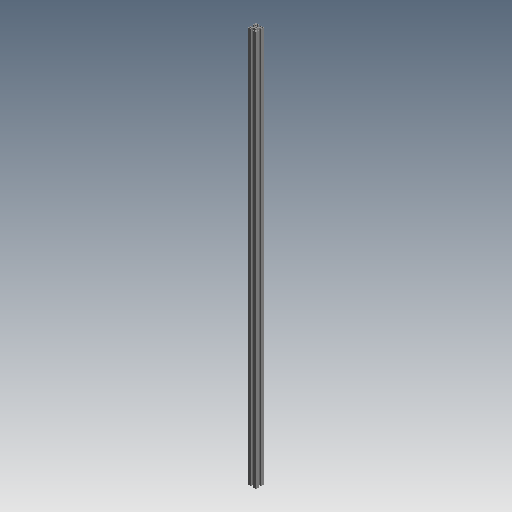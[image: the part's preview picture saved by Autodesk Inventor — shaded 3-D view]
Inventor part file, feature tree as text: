
AUTODESK INVENTOR PART (.ipt)
format: ipt  version: 2020 (Build 240168000, 168)  size: 211,968 bytes
history: native  units: mm (DEFAULTED — no unit token found)
features: other x21, sketch x3, hole x2, extrude x1, pattern_linear x1
ambient origin geometry x8: Origin, YZ Plane, XZ Plane, XY Plane, X Axis, Y Axis, Z Axis, Center Point
bodies: Solid1 (feature_tree)
feature tree (28):
  extrude  "Extrusion1"  Depth=1500.0mm
  hole  "Hole1"  [1 undecoded]
  hole  "Hole2"  [1 undecoded]
  pattern_linear  "Rectangular Pattern1"  [2 undecoded]
  other  "C1_XY"
  other  "C1_YZ"
  other  "C1_ZX"
  other  "C1_X"
  other  "C1_Y"
  other  "C1_Z"
  other  "C1_Center"
  other  "to_frame_cap1_XY"
  other  "to_frame_cap1_YZ"
  other  "to_frame_cap1_ZX"
  other  "to_frame_cap1_X"
  other  "to_frame_cap1_Y"
  other  "to_frame_cap1_Z"
  other  "to_frame_cap1_Center"
  other  "to_frame_cap2_XY"
  other  "to_frame_cap2_YZ"
  other  "to_frame_cap2_ZX"
  other  "to_frame_cap2_X"
  other  "to_frame_cap2_Y"
  other  "to_frame_cap2_Z"
  other  "to_frame_cap2_Center"
  sketch  "Sketch_1"  dims[d0=1500.0mm d1=0.0mm]
  sketch  "Sketch2"  dims[d2=6.8mm d3=6.0mm d4=4.0mm d5=2.0mm d6=90.0deg d7=1500.0mm d8=0.0mm]
  sketch  "Sketch3"  dims[d9=4.2mm d10=6.0mm d11=4.0mm d12=2.0mm d13=90.0deg d14=1500.0mm d15=0.0mm d16=20.0mm d18=23.2mm d19=20.0mm d21=23.2mm d22=0.0mm d23=0.0mm d24=0.0mm]
note: 4 required parameter values undecoded (feature->parameter linkage not recoverable at this tier; creation-order binding heuristic only, values carry confidence <= 0.55)
